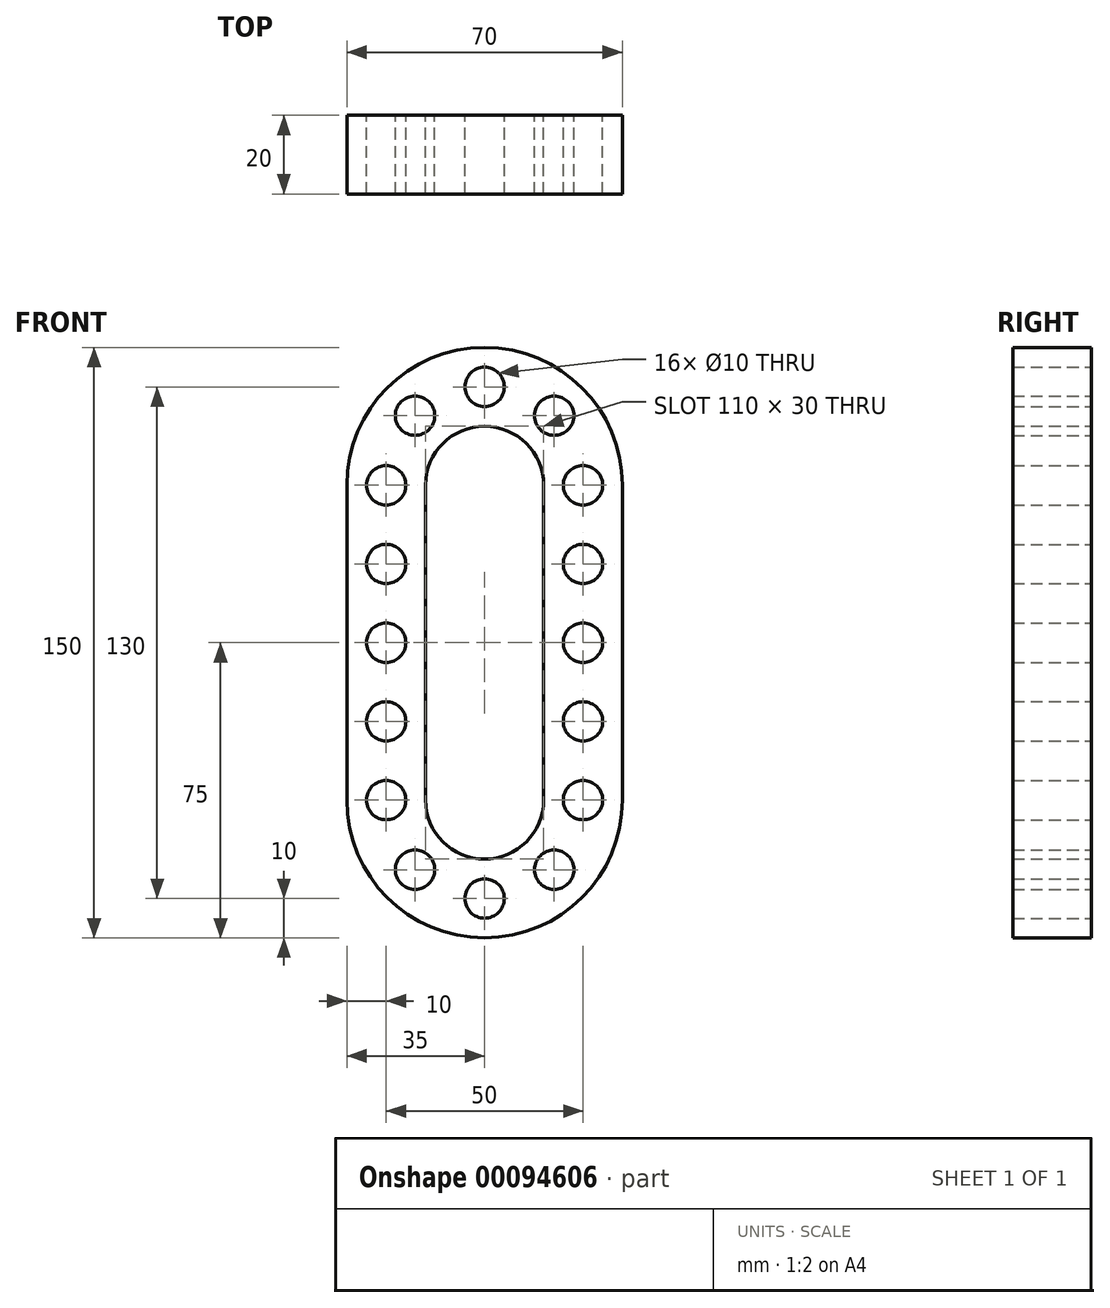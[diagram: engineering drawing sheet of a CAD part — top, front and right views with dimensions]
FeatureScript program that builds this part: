
annotation { "Feature Type Name" : "Feature", "Feature Type Description" : "" }
export const myFeature = defineFeature(function(context is Context, id is Id, definition is map)
    precondition{}
    {
        {
            var Q0;
            Q0=qCreatedBy(makeId("Front.planeOp"),FACE);
            var sketch = newSketch(context, id + "F0", { "sketchPlane" : qUnion([Q0])});
            skPoint(sketch, "E0", {"position": v(-25, 40) * mm});
            skLineSegment(sketch, "E1", {"start": v(-25, 40) * mm, "end": v(-25, 0) * mm, "construction": true});
            skArc(sketch, "E2", {"start": v(0, 65) * mm, "mid": v(-17.68, 57.68) * mm, "end": v(-25, 40) * mm, "construction": true});
            skArc(sketch, "E3.0.startCap", {"start": v(-35, 40) * mm, "mid": v(-25, 50) * mm, "end": v(-15, 40) * mm, "construction": true});
            skArc(sketch, "E3.0.endCap", {"start": v(-15, 0) * mm, "mid": v(-25, -10) * mm, "end": v(-35, 0) * mm, "construction": true});
            skLineSegment(sketch, "E3.0.left", {"start": v(-15, 40) * mm, "end": v(-15, 0) * mm});
            skLineSegment(sketch, "E3.0.right", {"start": v(-35, 40) * mm, "end": v(-35, 0) * mm});
            skArc(sketch, "E3.1.startCap", {"start": v(0, 75) * mm, "mid": v(10, 65) * mm, "end": v(0, 55) * mm, "construction": true});
            skArc(sketch, "E3.1.endCap", {"start": v(-15, 40) * mm, "mid": v(-25, 30) * mm, "end": v(-35, 40) * mm, "construction": true});
            skArc(sketch, "E3.1.left", {"start": v(0, 55) * mm, "mid": v(-10.6, 50.6) * mm, "end": v(-15, 40) * mm});
            skArc(sketch, "E3.1.right", {"start": v(0, 75) * mm, "mid": v(-24.75, 64.75) * mm, "end": v(-35, 40) * mm});
            skCircle(sketch, "E4", {"center": v(-25, 40) * mm, "radius": 5 * mm});
            skCircle(sketch, "E5.0.1.0", {"center": v(-25, 20) * mm, "radius": 5 * mm});
            skCircle(sketch, "E5.0.2.0", {"center": v(-25, 0) * mm, "radius": 5 * mm});
            skLineSegment(sketch, "E5.direction1", {"start": v(-25, 40) * mm, "end": v(0, 40) * mm, "construction": true});
            skLineSegment(sketch, "E5.direction2", {"start": v(-25, 40) * mm, "end": v(-25, 20) * mm, "construction": true});
            skCircle(sketch, "E6.1.0", {"center": v(-17.68, 57.68) * mm, "radius": 5 * mm});
            skCircle(sketch, "E6.2.0", {"center": v(0, 65) * mm, "radius": 5 * mm});
            skLineSegment(sketch, "E6.anchor1", {"start": v(0, 40) * mm, "end": v(-25, 40) * mm, "construction": true});
            skLineSegment(sketch, "E6.anchor2", {"start": v(0, 40) * mm, "end": v(0, 65) * mm, "construction": true});
            skLineSegment(sketch, "E7", {"start": v(0, 75) * mm, "end": v(0, 55) * mm});
            skLineSegment(sketch, "E8", {"start": v(-35, 0) * mm, "end": v(-15, 0) * mm});
            skSolve(sketch);
        }
        {
            var Q0;
            {var subQ8=sQuery(id+"F0.wireOp",EDGE,"E3.0.left");Q0=makeQuery(id+"F0.imprint","IMPRINT",FACE,{"disambiguationData":[TD([[makeQuery(id+"F0.imprint","IMPRINT",EDGE,{"derivedFrom":subQ8}),-1.0]])]});}
            extrude(context, id + "F1", {"entities" : qUnion([Q0]), "depth" : 20 * mm});
        }
        {
            var Q0;
            Q0=makeQuery(id+"F1.opExtrude","SWEPT_BODY",BODY,{"disambiguationData":[OSD([sQuery(id+"F0.wireOp",EDGE,"E3.0.left"),sQuery(id+"F0.wireOp",EDGE,"E3.0.right"),sQuery(id+"F0.wireOp",EDGE,"E3.1.left"),sQuery(id+"F0.wireOp",EDGE,"E3.1.right"),sQuery(id+"F0.wireOp",EDGE,"E4"),sQuery(id+"F0.wireOp",EDGE,"E5.0.1.0"),sQuery(id+"F0.wireOp",EDGE,"E5.0.2.0"),sQuery(id+"F0.wireOp",EDGE,"E6.1.0"),sQuery(id+"F0.wireOp",EDGE,"E6.2.0"),sQuery(id+"F0.wireOp",EDGE,"E7"),sQuery(id+"F0.wireOp",EDGE,"E8")])]});
            var Q1;
            Q1=qCreatedBy(makeId("Right.planeOp"),FACE);
            mirror(context, id + "F2", {"operationType" : NewBodyOperationType.ADD, "entities" : qUnion([Q0]), "mirrorPlane" : qUnion([Q1])});
        }
        {
            var Q0;
            Q0=makeQuery(id+"F1.opExtrude","SWEPT_BODY",BODY,{"disambiguationData":[OSD([sQuery(id+"F0.wireOp",EDGE,"E3.0.left"),sQuery(id+"F0.wireOp",EDGE,"E3.0.right"),sQuery(id+"F0.wireOp",EDGE,"E3.1.left"),sQuery(id+"F0.wireOp",EDGE,"E3.1.right"),sQuery(id+"F0.wireOp",EDGE,"E4"),sQuery(id+"F0.wireOp",EDGE,"E5.0.1.0"),sQuery(id+"F0.wireOp",EDGE,"E5.0.2.0"),sQuery(id+"F0.wireOp",EDGE,"E6.1.0"),sQuery(id+"F0.wireOp",EDGE,"E6.2.0"),sQuery(id+"F0.wireOp",EDGE,"E7"),sQuery(id+"F0.wireOp",EDGE,"E8")])]});
            var Q1;
            Q1=qCreatedBy(makeId("Top.planeOp"),FACE);
            mirror(context, id + "F3", {"operationType" : NewBodyOperationType.ADD, "entities" : qUnion([Q0]), "mirrorPlane" : qUnion([Q1])});
        }
    });
